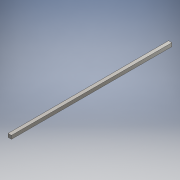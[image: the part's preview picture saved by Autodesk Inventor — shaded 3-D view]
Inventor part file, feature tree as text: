
AUTODESK INVENTOR PART (.ipt)
format: ipt  version: 2016 (Build 200138000, 138)  size: 91,136 bytes
history: native  units: mm
features: extrude x1, sketch x1
ambient origin geometry x8: Origin, YZ Plane, XZ Plane, XY Plane, X Axis, Y Axis, Z Axis, Center Point
bodies: Solid1 (feature_tree)
feature tree (2):
  extrude  "Extrusion1"  Depth=200.0mm
  sketch  "Sketch1"  dims[d0=9440.0mm d1=200.0mm d2=200.0mm d3=0.0mm]
